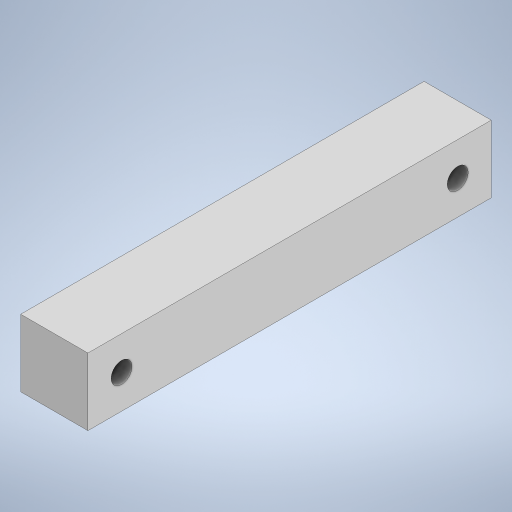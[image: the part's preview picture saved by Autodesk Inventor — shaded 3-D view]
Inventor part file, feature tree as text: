
AUTODESK INVENTOR PART (.ipt)
format: ipt  version: 2023 (Build 270158000, 158)  size: 212,992 bytes
history: native  units: mm
features: sketch x2, other x1, extrude x1, hole x1
ambient origin geometry x8: Origin, YZ Plane, XZ Plane, XY Plane, X Axis, Y Axis, Z Axis, Center Point
bodies: Body1 (feature_tree)
feature tree (5):
  other  "ソリッド1"
  extrude  "押し出し1"  Depth=10.0mm
  hole  "穴1"  [1 undecoded]
  sketch  "スケッチ1"
  sketch  "スケッチ2"
note: 1 required parameter value undecoded (feature->parameter linkage not recoverable at this tier; creation-order binding heuristic only, values carry confidence <= 0.55)
